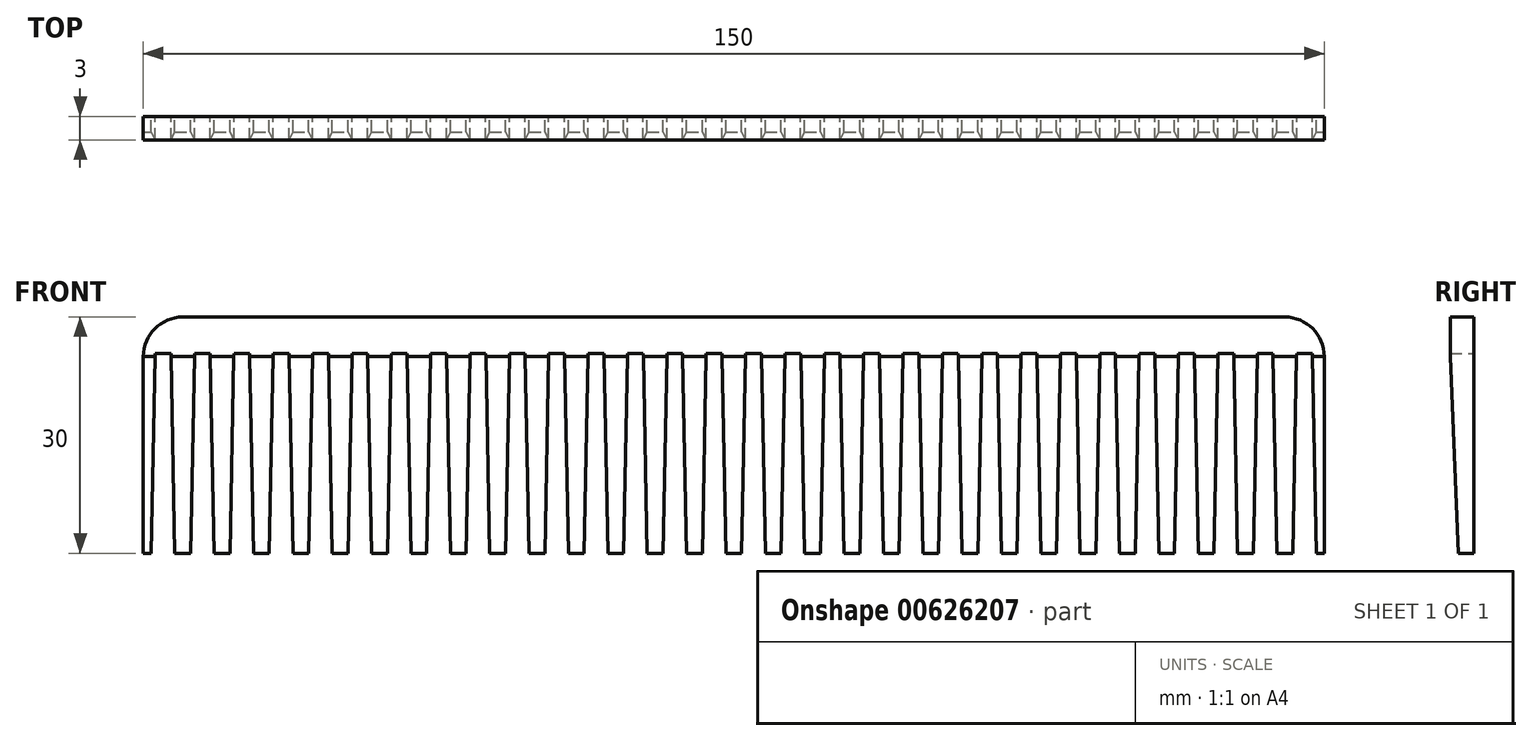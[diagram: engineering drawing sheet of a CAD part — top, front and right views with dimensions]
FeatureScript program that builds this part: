
annotation { "Feature Type Name" : "Feature", "Feature Type Description" : "" }
export const myFeature = defineFeature(function(context is Context, id is Id, definition is map)
    precondition{}
    {
        {
            var Q0;
            Q0=qCreatedBy(makeId("Front.planeOp"),FACE);
            var sketch = newSketch(context, id + "F0", { "sketchPlane" : qUnion([Q0])});
            skLineSegment(sketch, "E0.bottom", {"start": v(0, 0) * mm, "end": v(75, 0) * mm});
            skLineSegment(sketch, "E0.top", {"start": v(0, 30) * mm, "end": v(75, 30) * mm});
            skLineSegment(sketch, "E0.left", {"start": v(0, 0) * mm, "end": v(0, 30) * mm});
            skLineSegment(sketch, "E0.right", {"start": v(75, 0) * mm, "end": v(75, 30) * mm});
            skLineSegment(sketch, "E1", {"start": v(1, 0) * mm, "end": v(1.5, 25.36) * mm});
            skLineSegment(sketch, "E2", {"start": v(3.5, 25.36) * mm, "end": v(1.5, 25.36) * mm});
            skLineSegment(sketch, "E3", {"start": v(3.5, 25.36) * mm, "end": v(4, 0) * mm});
            skLineSegment(sketch, "E4", {"start": v(2.5, 25.36) * mm, "end": v(2.5, 0) * mm, "construction": true});
            skLineSegment(sketch, "E5.1.0.0", {"start": v(6, 0) * mm, "end": v(6.5, 25.36) * mm});
            skLineSegment(sketch, "E5.1.0.1", {"start": v(8.5, 25.36) * mm, "end": v(6.5, 25.36) * mm});
            skLineSegment(sketch, "E5.1.0.2", {"start": v(8.5, 25.36) * mm, "end": v(9, 0) * mm});
            skLineSegment(sketch, "E5.2.0.0", {"start": v(11, 0) * mm, "end": v(11.5, 25.36) * mm});
            skLineSegment(sketch, "E5.2.0.1", {"start": v(13.5, 25.36) * mm, "end": v(11.5, 25.36) * mm});
            skLineSegment(sketch, "E5.2.0.2", {"start": v(13.5, 25.36) * mm, "end": v(14, 0) * mm});
            skLineSegment(sketch, "E5.3.0.0", {"start": v(16, 0) * mm, "end": v(16.5, 25.36) * mm});
            skLineSegment(sketch, "E5.3.0.1", {"start": v(18.5, 25.36) * mm, "end": v(16.5, 25.36) * mm});
            skLineSegment(sketch, "E5.3.0.2", {"start": v(18.5, 25.36) * mm, "end": v(19, 0) * mm});
            skLineSegment(sketch, "E5.4.0.0", {"start": v(21, 0) * mm, "end": v(21.5, 25.36) * mm});
            skLineSegment(sketch, "E5.4.0.1", {"start": v(23.5, 25.36) * mm, "end": v(21.5, 25.36) * mm});
            skLineSegment(sketch, "E5.4.0.2", {"start": v(23.5, 25.36) * mm, "end": v(24, 0) * mm});
            skLineSegment(sketch, "E5.5.0.0", {"start": v(26, 0) * mm, "end": v(26.5, 25.36) * mm});
            skLineSegment(sketch, "E5.5.0.1", {"start": v(28.5, 25.36) * mm, "end": v(26.5, 25.36) * mm});
            skLineSegment(sketch, "E5.5.0.2", {"start": v(28.5, 25.36) * mm, "end": v(29, 0) * mm});
            skLineSegment(sketch, "E5.6.0.0", {"start": v(31, 0) * mm, "end": v(31.5, 25.36) * mm});
            skLineSegment(sketch, "E5.6.0.1", {"start": v(33.5, 25.36) * mm, "end": v(31.5, 25.36) * mm});
            skLineSegment(sketch, "E5.6.0.2", {"start": v(33.5, 25.36) * mm, "end": v(34, 0) * mm});
            skLineSegment(sketch, "E5.7.0.0", {"start": v(36, 0) * mm, "end": v(36.5, 25.36) * mm});
            skLineSegment(sketch, "E5.7.0.1", {"start": v(38.5, 25.36) * mm, "end": v(36.5, 25.36) * mm});
            skLineSegment(sketch, "E5.7.0.2", {"start": v(38.5, 25.36) * mm, "end": v(39, 0) * mm});
            skLineSegment(sketch, "E5.8.0.0", {"start": v(41, 0) * mm, "end": v(41.5, 25.36) * mm});
            skLineSegment(sketch, "E5.8.0.1", {"start": v(43.5, 25.36) * mm, "end": v(41.5, 25.36) * mm});
            skLineSegment(sketch, "E5.8.0.2", {"start": v(43.5, 25.36) * mm, "end": v(44, 0) * mm});
            skLineSegment(sketch, "E5.9.0.0", {"start": v(46, 0) * mm, "end": v(46.5, 25.36) * mm});
            skLineSegment(sketch, "E5.9.0.1", {"start": v(48.5, 25.36) * mm, "end": v(46.5, 25.36) * mm});
            skLineSegment(sketch, "E5.9.0.2", {"start": v(48.5, 25.36) * mm, "end": v(49, 0) * mm});
            skLineSegment(sketch, "E5.10.0.0", {"start": v(51, 0) * mm, "end": v(51.5, 25.36) * mm});
            skLineSegment(sketch, "E5.10.0.1", {"start": v(53.5, 25.36) * mm, "end": v(51.5, 25.36) * mm});
            skLineSegment(sketch, "E5.10.0.2", {"start": v(53.5, 25.36) * mm, "end": v(54, 0) * mm});
            skLineSegment(sketch, "E5.11.0.0", {"start": v(56, 0) * mm, "end": v(56.5, 25.36) * mm});
            skLineSegment(sketch, "E5.11.0.1", {"start": v(58.5, 25.36) * mm, "end": v(56.5, 25.36) * mm});
            skLineSegment(sketch, "E5.11.0.2", {"start": v(58.5, 25.36) * mm, "end": v(59, 0) * mm});
            skLineSegment(sketch, "E5.12.0.0", {"start": v(61, 0) * mm, "end": v(61.5, 25.36) * mm});
            skLineSegment(sketch, "E5.12.0.1", {"start": v(63.5, 25.36) * mm, "end": v(61.5, 25.36) * mm});
            skLineSegment(sketch, "E5.12.0.2", {"start": v(63.5, 25.36) * mm, "end": v(64, 0) * mm});
            skLineSegment(sketch, "E5.13.0.0", {"start": v(66, 0) * mm, "end": v(66.5, 25.36) * mm});
            skLineSegment(sketch, "E5.13.0.1", {"start": v(68.5, 25.36) * mm, "end": v(66.5, 25.36) * mm});
            skLineSegment(sketch, "E5.13.0.2", {"start": v(68.5, 25.36) * mm, "end": v(69, 0) * mm});
            skLineSegment(sketch, "E5.14.0.0", {"start": v(71, 0) * mm, "end": v(71.5, 25.36) * mm});
            skLineSegment(sketch, "E5.14.0.1", {"start": v(73.5, 25.36) * mm, "end": v(71.5, 25.36) * mm});
            skLineSegment(sketch, "E5.14.0.2", {"start": v(73.5, 25.36) * mm, "end": v(74, 0) * mm});
            skLineSegment(sketch, "E5.direction1", {"start": v(1, 0) * mm, "end": v(6, 0) * mm, "construction": true});
            skSolve(sketch);
        }
        {
            var Q0;
            Q0=makeQuery(id+"F0.imprint","IMPRINT",FACE,{"disambiguationData":[TD([[makeQuery(id+"F0.imprint","IMPRINT",EDGE,{"derivedFrom":sQuery(id+"F0.wireOp",EDGE,"E0.top")}),-1.0]])]});
            extrude(context, id + "F1", {"entities" : qUnion([Q0]), "endBound" : BoundingType.SYMMETRIC, "depth" : 3 * mm, "offsetDistance" : 25 * mm});
        }
        {
            var Q0;
            Q0=makeQuery(id+"F1.opExtrude","SWEPT_EDGE",EDGE,{"disambiguationData":[OSD([sQuery(id+"F0.wireOp",EDGE,"E0.top"),sQuery(id+"F0.wireOp",EDGE,"E0.right")])]});
            fillet(context, id + "F2", {"entities" : qUnion([Q0]), "radius" : 5 * mm, "tangentPropagation" : true, "allowEdgeOverflow" : false});
        }
        {
            var Q0;
            Q0=qCreatedBy(makeId("Right.planeOp"),FACE);
            var sketch = newSketch(context, id + "F3", { "sketchPlane" : qUnion([Q0])});
            skLineSegment(sketch, "E6", {"start": v(-1.5, 24.96) * mm, "end": v(-0.49, 0) * mm});
            skLineSegment(sketch, "E7", {"start": v(-0.49, 0) * mm, "end": v(-1.52, 0) * mm});
            skLineSegment(sketch, "E8", {"start": v(-1.5, 24.96) * mm, "end": v(-1.52, 0) * mm});
            skSolve(sketch);
        }
        {
            var Q0;
            Q0=makeQuery(id+"F1.opExtrude","SWEPT_BODY",BODY,{"disambiguationData":[OSD([sQuery(id+"F0.wireOp",EDGE,"E0.bottom"),sQuery(id+"F0.wireOp",EDGE,"E0.top"),sQuery(id+"F0.wireOp",EDGE,"E0.left"),sQuery(id+"F0.wireOp",EDGE,"E0.right"),sQuery(id+"F0.wireOp",EDGE,"E1"),sQuery(id+"F0.wireOp",EDGE,"E2"),sQuery(id+"F0.wireOp",EDGE,"E3"),sQuery(id+"F0.wireOp",EDGE,"E5.1.0.0"),sQuery(id+"F0.wireOp",EDGE,"E5.1.0.1"),sQuery(id+"F0.wireOp",EDGE,"E5.1.0.2"),sQuery(id+"F0.wireOp",EDGE,"E5.2.0.0"),sQuery(id+"F0.wireOp",EDGE,"E5.2.0.1"),sQuery(id+"F0.wireOp",EDGE,"E5.2.0.2"),sQuery(id+"F0.wireOp",EDGE,"E5.3.0.0"),sQuery(id+"F0.wireOp",EDGE,"E5.3.0.1"),sQuery(id+"F0.wireOp",EDGE,"E5.3.0.2"),sQuery(id+"F0.wireOp",EDGE,"E5.4.0.0"),sQuery(id+"F0.wireOp",EDGE,"E5.4.0.1"),sQuery(id+"F0.wireOp",EDGE,"E5.4.0.2"),sQuery(id+"F0.wireOp",EDGE,"E5.5.0.0"),sQuery(id+"F0.wireOp",EDGE,"E5.5.0.1"),sQuery(id+"F0.wireOp",EDGE,"E5.5.0.2"),sQuery(id+"F0.wireOp",EDGE,"E5.6.0.0"),sQuery(id+"F0.wireOp",EDGE,"E5.6.0.1"),sQuery(id+"F0.wireOp",EDGE,"E5.6.0.2"),sQuery(id+"F0.wireOp",EDGE,"E5.7.0.0"),sQuery(id+"F0.wireOp",EDGE,"E5.7.0.1"),sQuery(id+"F0.wireOp",EDGE,"E5.7.0.2"),sQuery(id+"F0.wireOp",EDGE,"E5.8.0.0"),sQuery(id+"F0.wireOp",EDGE,"E5.8.0.1"),sQuery(id+"F0.wireOp",EDGE,"E5.8.0.2"),sQuery(id+"F0.wireOp",EDGE,"E5.9.0.0"),sQuery(id+"F0.wireOp",EDGE,"E5.9.0.1"),sQuery(id+"F0.wireOp",EDGE,"E5.9.0.2"),sQuery(id+"F0.wireOp",EDGE,"E5.10.0.0"),sQuery(id+"F0.wireOp",EDGE,"E5.10.0.1"),sQuery(id+"F0.wireOp",EDGE,"E5.10.0.2"),sQuery(id+"F0.wireOp",EDGE,"E5.11.0.0"),sQuery(id+"F0.wireOp",EDGE,"E5.11.0.1"),sQuery(id+"F0.wireOp",EDGE,"E5.11.0.2"),sQuery(id+"F0.wireOp",EDGE,"E5.12.0.0"),sQuery(id+"F0.wireOp",EDGE,"E5.12.0.1"),sQuery(id+"F0.wireOp",EDGE,"E5.12.0.2"),sQuery(id+"F0.wireOp",EDGE,"E5.13.0.0"),sQuery(id+"F0.wireOp",EDGE,"E5.13.0.1"),sQuery(id+"F0.wireOp",EDGE,"E5.13.0.2"),sQuery(id+"F0.wireOp",EDGE,"E5.14.0.0"),sQuery(id+"F0.wireOp",EDGE,"E5.14.0.1"),sQuery(id+"F0.wireOp",EDGE,"E5.14.0.2")])]});
            var Q1;
            Q1=makeQuery(id+"F1.opExtrude","SWEPT_FACE",FACE,{"disambiguationData":[OSD([sQuery(id+"F0.wireOp",EDGE,"E0.left")])]});
            mirror(context, id + "F4", {"operationType" : NewBodyOperationType.ADD, "entities" : qUnion([Q0]), "mirrorPlane" : qUnion([Q1])});
        }
        {
            var Q0;
            Q0=makeQuery(id+"F3.imprint","IMPRINT",FACE,{"disambiguationData":[TD([[makeQuery(id+"F3.imprint","IMPRINT",EDGE,{"derivedFrom":sQuery(id+"F3.wireOp",EDGE,"E6")}),-1.0]])]});
            extrude(context, id + "F5", {"entities" : qUnion([Q0]), "operationType" : NewBodyOperationType.REMOVE, "endBound" : BoundingType.SYMMETRIC, "oppositeDirection" : true, "depth" : 200 * mm, "offsetDistance" : 25 * mm});
        }
    });
